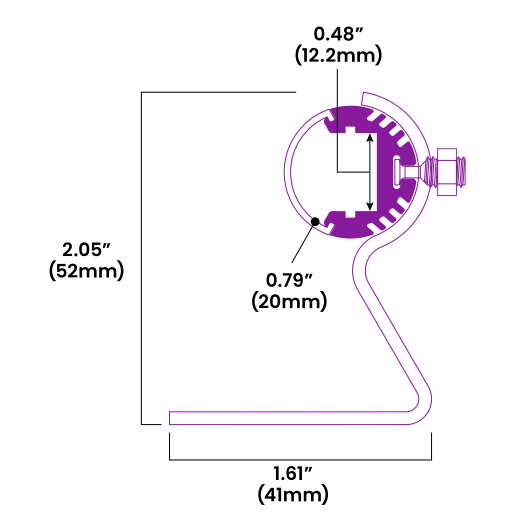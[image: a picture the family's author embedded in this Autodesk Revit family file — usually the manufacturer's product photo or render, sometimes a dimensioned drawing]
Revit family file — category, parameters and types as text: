
# Revit family: S2020 updated 2
name_source: partatom
category: Lighting Fixtures
units: mm (PartAtom-declared; Revit-internal decimal feet)

## family parameters
Cut with Voids When Loaded = No
Host = Face
Light Source = No
Part Type = Normal
Room Calculation Point = No
Round Connector Dimension = Use Diameter
Shared = Yes

## types (4) — shared parameters
Current Amps = 50 A
Default Elevation = 48 "
Description = Flexible, Linear LED Lighting
Environment = Indoor
Frequency = 60 Hz
Has Battery Backup = No
Has Dimming = Yes
Housing Protection Rating = Consult Manufacturer Website for more Information
Initial Color Comments = Perfomance based on 3000K Photometric Web File
Initial Intensity Comments = Refer LED Strip type for Lumen Value
Input Voltage = 24VDC
LED Tape Page URL = https://bllighting.com
LED finish = LED
LED strip = Strip
LED tape Documentation Link = https://bllighting.com
Lamp Life = 50,000 Hours
Lens Material = Polycarbonate Optic
Load Classification = Lighting
Manufacturer = BL Lighting
Mounting Method = Surface Mount
Number of Poles = 1
Operating Temperature = Consult Manufacturer Website for more Information
Phase = 1
Power Factor = 1
Power Source Type = Driver
Product Documentation Link = https://bllighting.com
Product Page URL = https://bllighting.com
Profile Material = Alumnium Base Track
URL = https://bllighting.com
Version = 2020-v2.9
Voltage = 24 V
Warranty URL = https://bllighting.com

## per-type parameters (varying)
| type | Apparent Load | CCT | Color Option Available | D2 | D3 | DFD2 | DFD3 | Increment | Lamp | Lumen Output | Max Input Current | Model | Number of LED's | Product Name | Wattage Comments |
| 209 lm per FT 3.0W per FT - D2 | 120 VA | 2400K,2700K,3000K,3500K,4000K,5000K,RED,GREEN,BLUE,AMBER | 2400K,2700K,3000K,3500K,4000K,5000K,RED,GREEN,BLUE,AMBER | Yes | No | No | No | 1.9685 " | LED,SMD 3528 | 209 lm/FT | 5A | D2 | 36 Diodes/FT | D2 | 3.0W/FT |
| 370 lm per FT 5.5 W per FT - D3 | 120 VA | 2700K,3000K,3500K,4000K,6000K | 2700K,3000K,3500K,4000K,6000K | No | Yes | No | No | 2.4803 " | LED,SMD 5060 | 370 lm/FT | 5A | D3 | 30 Diodes/FT | D3 | 5.5 W/FT |
| 258 lm per FT 2.44 W per FT - DFD2 | 96 VA | 2400K,2700K,3000K,3500K,4000K | 2400K,2700K,3000K,3500K,4000K | No | No | Yes | No | 1.9685 " |  | 258 lm/FT | 4A | DFD2 | 146 Diodes/FT | DFD2 | 2.44W/FT |
| 419 lm per FT 4.4 W per FT - DFD3 | 96 VA | 2400K,2700K,3000K,3500K,4000K | 2400K,2700K,3000K,3500K,4000K | No | No | No | Yes | 1.9685 " |  | 419 lm/FT | 4A | DFD3 | 146 Diodes/FT | DFD3 | 4.4W/FT |

## geometry (parser evidence)
native form markers: Sweep x51
no freeform markers — native parametric forms only
